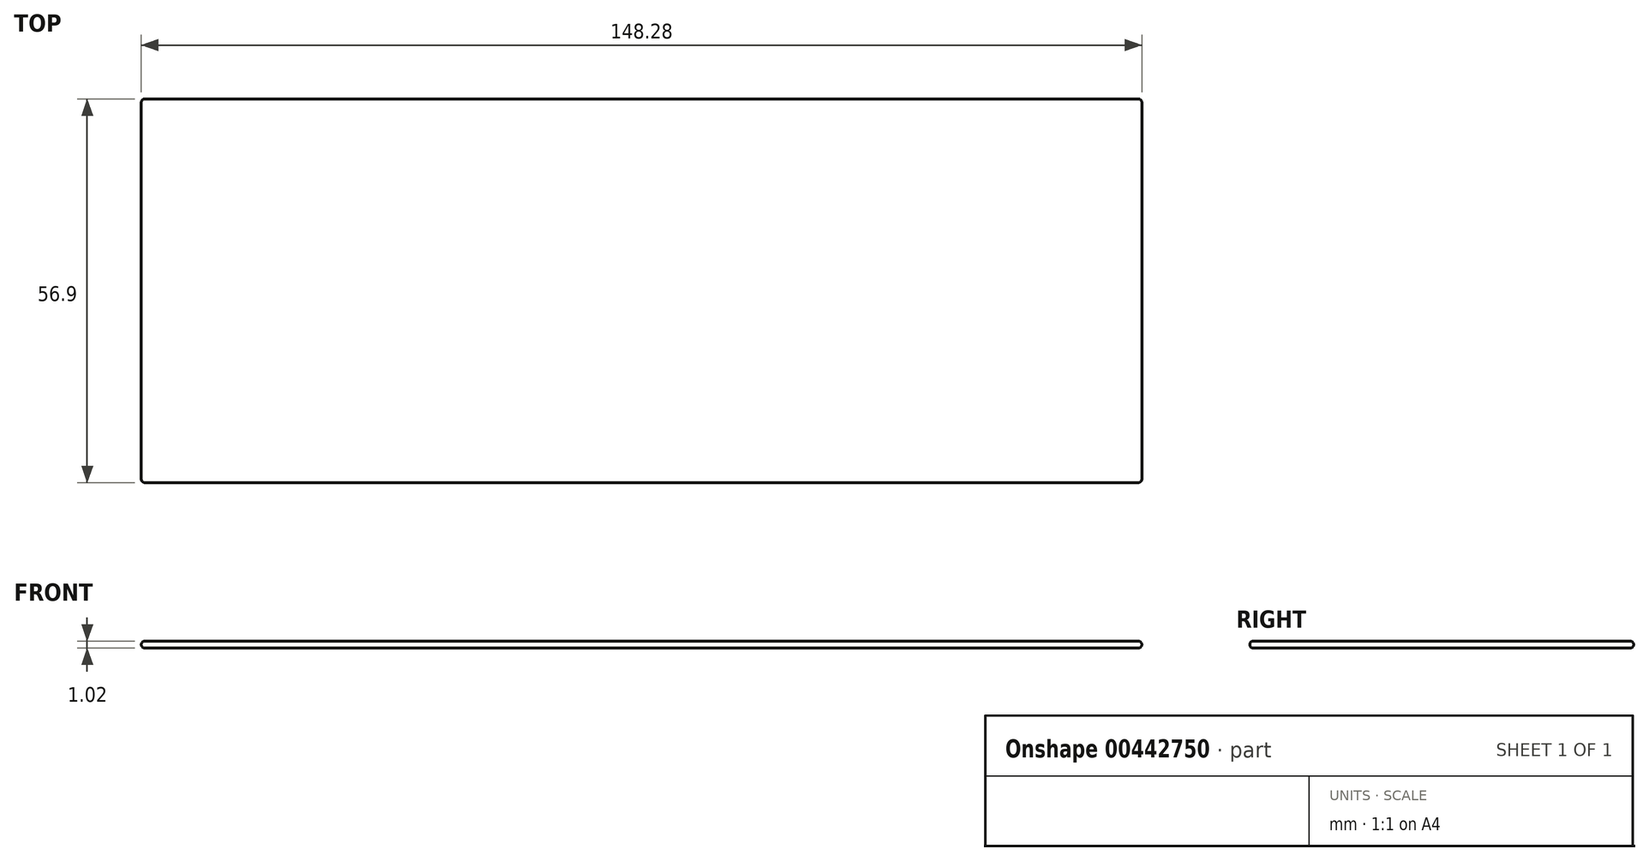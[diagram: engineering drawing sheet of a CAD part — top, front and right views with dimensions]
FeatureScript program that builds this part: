
annotation { "Feature Type Name" : "Feature", "Feature Type Description" : "" }
export const myFeature = defineFeature(function(context is Context, id is Id, definition is map)
    precondition{}
    {
        {
            var Q0;
            Q0=qCreatedBy(makeId("Top.planeOp"),FACE);
            var sketch = newSketch(context, id + "F0", { "sketchPlane" : qUnion([Q0])});
            skLineSegment(sketch, "E0.bottom", {"start": v(74.14, -28.45) * mm, "end": v(-74.14, -28.45) * mm});
            skLineSegment(sketch, "E0.top", {"start": v(74.14, 28.45) * mm, "end": v(-74.14, 28.45) * mm});
            skLineSegment(sketch, "E0.left", {"start": v(74.14, -28.45) * mm, "end": v(74.14, 28.45) * mm});
            skLineSegment(sketch, "E0.right", {"start": v(-74.14, -28.45) * mm, "end": v(-74.14, 28.45) * mm});
            skPoint(sketch, "E0.middle", {"position": v(0, 0) * mm});
            skSolve(sketch);
        }
        {
            var Q0;
            Q0 = qSketchRegion(id + "F0", true);
            extrude(context, id + "F1", {"entities" : qUnion([Q0]), "depth" : 1.02 * mm, "offsetDistance" : 25.4 * mm});
        }
        {
            var Q0;
            Q0=makeQuery(id+"F1.opExtrude","SWEPT_FACE",FACE,{"disambiguationData":[OSD([sQuery(id+"F0.wireOp",EDGE,"E0.bottom")])]});
            var Q1;
            Q1=makeQuery(id+"F1.opExtrude","SWEPT_FACE",FACE,{"disambiguationData":[OSD([sQuery(id+"F0.wireOp",EDGE,"E0.right")])]});
            var Q2;
            Q2=makeQuery(id+"F1.opExtrude","SWEPT_FACE",FACE,{"disambiguationData":[OSD([sQuery(id+"F0.wireOp",EDGE,"E0.top")])]});
            var Q3;
            Q3=makeQuery(id+"F1.opExtrude","SWEPT_FACE",FACE,{"disambiguationData":[OSD([sQuery(id+"F0.wireOp",EDGE,"E0.left")])]});
            fillet(context, id + "F2", {"entities" : qUnion([Q0, Q1, Q2, Q3]), "radius" : 0.5 * mm, "tangentPropagation" : true, "allowEdgeOverflow" : false});
        }
    });
